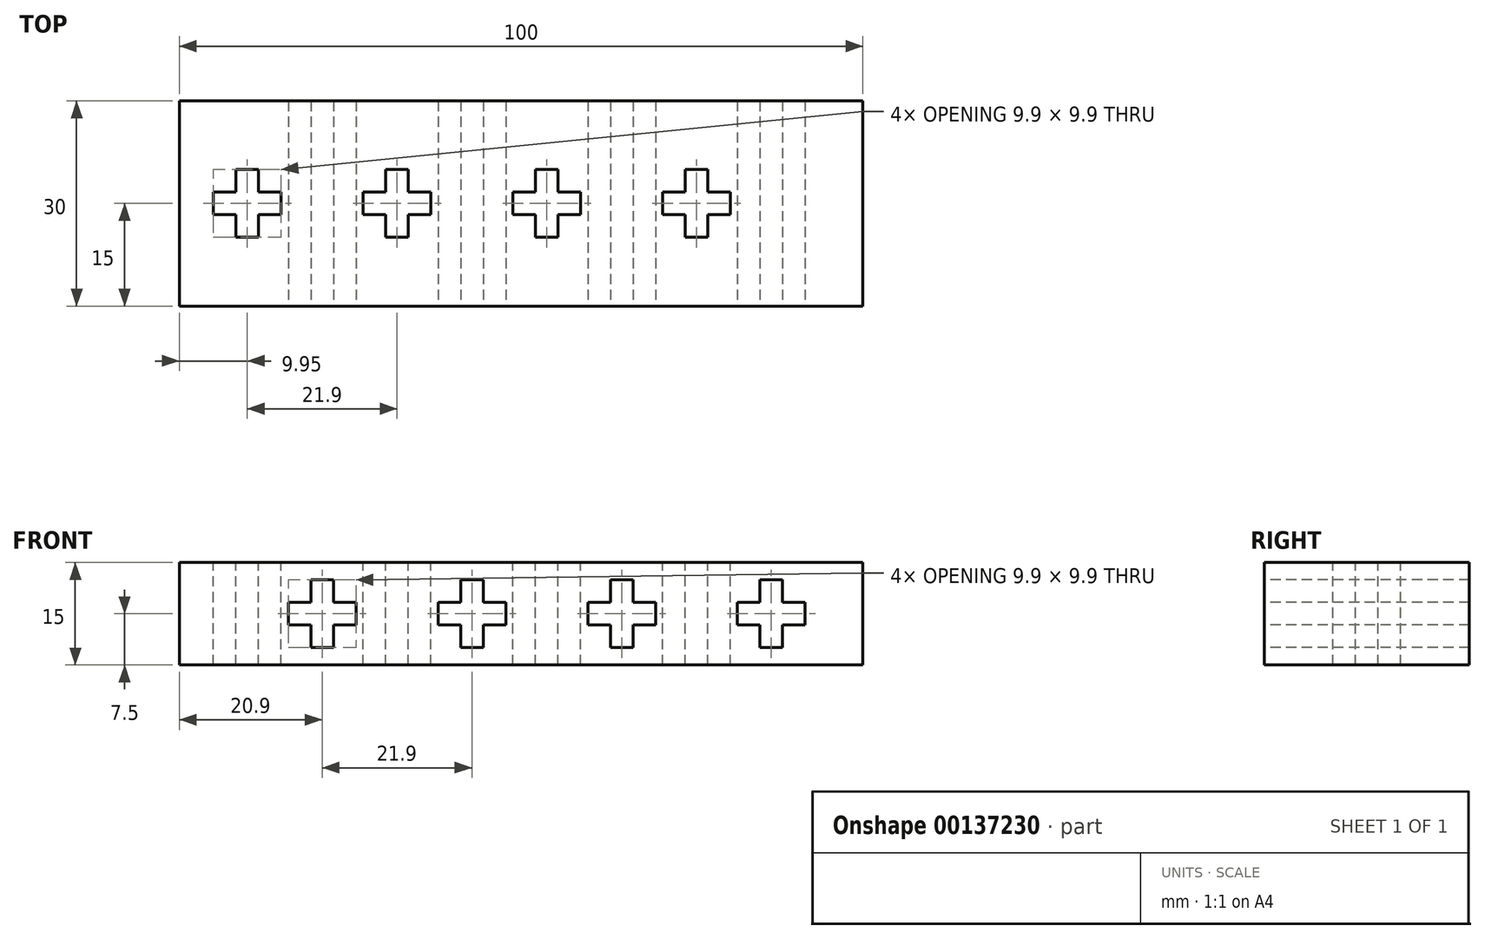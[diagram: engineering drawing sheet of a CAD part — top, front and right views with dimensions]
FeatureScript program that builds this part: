
annotation { "Feature Type Name" : "Feature", "Feature Type Description" : "" }
export const myFeature = defineFeature(function(context is Context, id is Id, definition is map)
    precondition{}
    {
        {
            var Q0;
            Q0=qCreatedBy(makeId("Top.planeOp"),FACE);
            var sketch = newSketch(context, id + "F0", { "sketchPlane" : qUnion([Q0])});
            skLineSegment(sketch, "E0.bottom", {"start": v(-50, 15) * mm, "end": v(50, 15) * mm});
            skLineSegment(sketch, "E0.top", {"start": v(-50, -15) * mm, "end": v(50, -15) * mm});
            skLineSegment(sketch, "E0.left", {"start": v(-50, 15) * mm, "end": v(-50, -15) * mm});
            skLineSegment(sketch, "E0.right", {"start": v(50, 15) * mm, "end": v(50, -15) * mm});
            skPoint(sketch, "E0.middle", {"position": v(0, 0) * mm});
            skSolve(sketch);
        }
        {
            var Q0;
            Q0 = qSketchRegion(id + "F0", true);
            extrude(context, id + "F1", {"entities" : qUnion([Q0]), "depth" : 15 * mm});
        }
        {
            var Q0;
            Q0=makeQuery(id+"F1.opExtrude","CAP_FACE",FACE,{"disambiguationData":[OSD([sQuery(id+"F0.wireOp",EDGE,"E0.bottom"),sQuery(id+"F0.wireOp",EDGE,"E0.top"),sQuery(id+"F0.wireOp",EDGE,"E0.left"),sQuery(id+"F0.wireOp",EDGE,"E0.right")])],"isStart":false});
            var sketch = newSketch(context, id + "F2", { "sketchPlane" : qUnion([Q0])});
            skLineSegment(sketch, "E1.bottom", {"start": v(-41.7, 4.95) * mm, "end": v(-38.4, 4.95) * mm});
            skLineSegment(sketch, "E1.top", {"start": v(-41.7, -4.95) * mm, "end": v(-38.4, -4.95) * mm});
            skLineSegment(sketch, "E1.left", {"start": v(-41.7, 4.95) * mm, "end": v(-41.7, 1.65) * mm});
            skLineSegment(sketch, "E1.right", {"start": v(-38.4, 4.95) * mm, "end": v(-38.4, 1.65) * mm});
            skPoint(sketch, "E1.middle", {"position": v(-40.05, 0) * mm});
            skLineSegment(sketch, "E2.bottom", {"start": v(-45, 1.65) * mm, "end": v(-41.7, 1.65) * mm});
            skLineSegment(sketch, "E2.top", {"start": v(-45, -1.65) * mm, "end": v(-41.7, -1.65) * mm});
            skLineSegment(sketch, "E2.left", {"start": v(-45, 1.65) * mm, "end": v(-45, -1.65) * mm});
            skLineSegment(sketch, "E2.right", {"start": v(-35.1, 1.65) * mm, "end": v(-35.1, -1.65) * mm});
            skLineSegment(sketch, "E3.trimOffspring", {"start": v(-41.7, -1.65) * mm, "end": v(-41.7, -4.95) * mm});
            skLineSegment(sketch, "E4.trimOffspring", {"start": v(-38.4, 1.65) * mm, "end": v(-35.1, 1.65) * mm});
            skLineSegment(sketch, "E5.trimOffspring", {"start": v(-38.4, -1.65) * mm, "end": v(-38.4, -4.95) * mm});
            skLineSegment(sketch, "E6.trimOffspring", {"start": v(-38.4, -1.65) * mm, "end": v(-35.1, -1.65) * mm});
            skPoint(sketch, "E7.1.0.0", {"position": v(-18.15, 0) * mm});
            skLineSegment(sketch, "E7.1.0.1", {"start": v(-23.1, -1.65) * mm, "end": v(-19.8, -1.65) * mm});
            skLineSegment(sketch, "E7.1.0.2", {"start": v(-16.5, -1.65) * mm, "end": v(-13.2, -1.65) * mm});
            skLineSegment(sketch, "E7.1.0.3", {"start": v(-16.5, -1.65) * mm, "end": v(-16.5, -4.95) * mm});
            skLineSegment(sketch, "E7.1.0.4", {"start": v(-16.5, 4.95) * mm, "end": v(-16.5, 1.65) * mm});
            skLineSegment(sketch, "E7.1.0.5", {"start": v(-19.8, 4.95) * mm, "end": v(-19.8, 1.65) * mm});
            skLineSegment(sketch, "E7.1.0.6", {"start": v(-19.8, -4.95) * mm, "end": v(-16.5, -4.95) * mm});
            skLineSegment(sketch, "E7.1.0.7", {"start": v(-19.8, 4.95) * mm, "end": v(-16.5, 4.95) * mm});
            skLineSegment(sketch, "E7.1.0.8", {"start": v(-16.5, 1.65) * mm, "end": v(-13.2, 1.65) * mm});
            skLineSegment(sketch, "E7.1.0.9", {"start": v(-23.1, 1.65) * mm, "end": v(-19.8, 1.65) * mm});
            skLineSegment(sketch, "E7.1.0.10", {"start": v(-19.8, -1.65) * mm, "end": v(-19.8, -4.95) * mm});
            skLineSegment(sketch, "E7.1.0.11", {"start": v(-23.1, 1.65) * mm, "end": v(-23.1, -1.65) * mm});
            skLineSegment(sketch, "E7.1.0.12", {"start": v(-13.2, 1.65) * mm, "end": v(-13.2, -1.65) * mm});
            skPoint(sketch, "E7.1.0.13", {"position": v(-18.15, 0) * mm});
            skPoint(sketch, "E7.2.0.0", {"position": v(3.75, 0) * mm});
            skLineSegment(sketch, "E7.2.0.1", {"start": v(-1.2, -1.65) * mm, "end": v(2.1, -1.65) * mm});
            skLineSegment(sketch, "E7.2.0.2", {"start": v(5.4, -1.65) * mm, "end": v(8.7, -1.65) * mm});
            skLineSegment(sketch, "E7.2.0.3", {"start": v(5.4, -1.65) * mm, "end": v(5.4, -4.95) * mm});
            skLineSegment(sketch, "E7.2.0.4", {"start": v(5.4, 4.95) * mm, "end": v(5.4, 1.65) * mm});
            skLineSegment(sketch, "E7.2.0.5", {"start": v(2.1, 4.95) * mm, "end": v(2.1, 1.65) * mm});
            skLineSegment(sketch, "E7.2.0.6", {"start": v(2.1, -4.95) * mm, "end": v(5.4, -4.95) * mm});
            skLineSegment(sketch, "E7.2.0.7", {"start": v(2.1, 4.95) * mm, "end": v(5.4, 4.95) * mm});
            skLineSegment(sketch, "E7.2.0.8", {"start": v(5.4, 1.65) * mm, "end": v(8.7, 1.65) * mm});
            skLineSegment(sketch, "E7.2.0.9", {"start": v(-1.2, 1.65) * mm, "end": v(2.1, 1.65) * mm});
            skLineSegment(sketch, "E7.2.0.10", {"start": v(2.1, -1.65) * mm, "end": v(2.1, -4.95) * mm});
            skLineSegment(sketch, "E7.2.0.11", {"start": v(-1.2, 1.65) * mm, "end": v(-1.2, -1.65) * mm});
            skLineSegment(sketch, "E7.2.0.12", {"start": v(8.7, 1.65) * mm, "end": v(8.7, -1.65) * mm});
            skPoint(sketch, "E7.2.0.13", {"position": v(3.75, 0) * mm});
            skPoint(sketch, "E7.3.0.0", {"position": v(25.65, 0) * mm});
            skLineSegment(sketch, "E7.3.0.1", {"start": v(20.7, -1.65) * mm, "end": v(24, -1.65) * mm});
            skLineSegment(sketch, "E7.3.0.2", {"start": v(27.3, -1.65) * mm, "end": v(30.6, -1.65) * mm});
            skLineSegment(sketch, "E7.3.0.3", {"start": v(27.3, -1.65) * mm, "end": v(27.3, -4.95) * mm});
            skLineSegment(sketch, "E7.3.0.4", {"start": v(27.3, 4.95) * mm, "end": v(27.3, 1.65) * mm});
            skLineSegment(sketch, "E7.3.0.5", {"start": v(24, 4.95) * mm, "end": v(24, 1.65) * mm});
            skLineSegment(sketch, "E7.3.0.6", {"start": v(24, -4.95) * mm, "end": v(27.3, -4.95) * mm});
            skLineSegment(sketch, "E7.3.0.7", {"start": v(24, 4.95) * mm, "end": v(27.3, 4.95) * mm});
            skLineSegment(sketch, "E7.3.0.8", {"start": v(27.3, 1.65) * mm, "end": v(30.6, 1.65) * mm});
            skLineSegment(sketch, "E7.3.0.9", {"start": v(20.7, 1.65) * mm, "end": v(24, 1.65) * mm});
            skLineSegment(sketch, "E7.3.0.10", {"start": v(24, -1.65) * mm, "end": v(24, -4.95) * mm});
            skLineSegment(sketch, "E7.3.0.11", {"start": v(20.7, 1.65) * mm, "end": v(20.7, -1.65) * mm});
            skLineSegment(sketch, "E7.3.0.12", {"start": v(30.6, 1.65) * mm, "end": v(30.6, -1.65) * mm});
            skPoint(sketch, "E7.3.0.13", {"position": v(25.65, 0) * mm});
            skLineSegment(sketch, "E7.direction1", {"start": v(-45, 1.65) * mm, "end": v(-23.1, 1.65) * mm, "construction": true});
            skSolve(sketch);
        }
        {
            var Q0;
            Q0 = qSketchRegion(id + "F2", true);
            extrude(context, id + "F3", {"entities" : qUnion([Q0]), "operationType" : NewBodyOperationType.REMOVE, "endBound" : BoundingType.THROUGH_ALL, "oppositeDirection" : true, "depth" : 25 * mm});
        }
        {
            var Q0;
            Q0=makeQuery(id+"F1.opExtrude","SWEPT_FACE",FACE,{"disambiguationData":[OSD([sQuery(id+"F0.wireOp",EDGE,"E0.top")])]});
            var sketch = newSketch(context, id + "F4", { "sketchPlane" : qUnion([Q0])});
            skLineSegment(sketch, "E8", {"start": v(-50, 7.5) * mm, "end": v(50, 7.5) * mm, "construction": true});
            skLineSegment(sketch, "E9.bottom", {"start": v(-30.75, 12.45) * mm, "end": v(-27.45, 12.45) * mm});
            skLineSegment(sketch, "E9.top", {"start": v(-30.75, 2.55) * mm, "end": v(-27.45, 2.55) * mm});
            skLineSegment(sketch, "E9.left", {"start": v(-30.75, 12.45) * mm, "end": v(-30.75, 9.15) * mm});
            skPoint(sketch, "E9.middle", {"position": v(-29.1, 7.5) * mm});
            skLineSegment(sketch, "E10.bottom", {"start": v(-34.05, 9.15) * mm, "end": v(-30.75, 9.15) * mm});
            skLineSegment(sketch, "E10.top", {"start": v(-34.05, 5.85) * mm, "end": v(-30.75, 5.85) * mm});
            skLineSegment(sketch, "E10.left", {"start": v(-34.05, 9.15) * mm, "end": v(-34.05, 5.85) * mm});
            skLineSegment(sketch, "E10.right", {"start": v(-24.15, 9.15) * mm, "end": v(-24.15, 5.85) * mm});
            skLineSegment(sketch, "E11.trimOffspring", {"start": v(-30.75, 5.85) * mm, "end": v(-30.75, 2.55) * mm});
            skLineSegment(sketch, "E12.trimOffspring", {"start": v(-27.45, 9.15) * mm, "end": v(-24.15, 9.15) * mm});
            skLineSegment(sketch, "E13.trimOffspring", {"start": v(-27.45, 5.85) * mm, "end": v(-27.45, 2.55) * mm});
            skLineSegment(sketch, "E14.trimOffspring", {"start": v(-27.45, 5.85) * mm, "end": v(-24.15, 5.85) * mm});
            skLineSegment(sketch, "E15", {"start": v(-27.45, 12.45) * mm, "end": v(-27.45, 9.15) * mm});
            skPoint(sketch, "E16.1.0.0", {"position": v(-7.2, 7.5) * mm});
            skLineSegment(sketch, "E16.1.0.1", {"start": v(-12.15, 9.15) * mm, "end": v(-12.15, 5.85) * mm});
            skLineSegment(sketch, "E16.1.0.2", {"start": v(-5.55, 12.45) * mm, "end": v(-5.55, 9.15) * mm});
            skLineSegment(sketch, "E16.1.0.3", {"start": v(-12.15, 9.15) * mm, "end": v(-8.85, 9.15) * mm});
            skLineSegment(sketch, "E16.1.0.4", {"start": v(-5.55, 5.85) * mm, "end": v(-2.25, 5.85) * mm});
            skLineSegment(sketch, "E16.1.0.5", {"start": v(-8.85, 12.45) * mm, "end": v(-5.55, 12.45) * mm});
            skLineSegment(sketch, "E16.1.0.6", {"start": v(-5.55, 5.85) * mm, "end": v(-5.55, 2.55) * mm});
            skLineSegment(sketch, "E16.1.0.7", {"start": v(-8.85, 12.45) * mm, "end": v(-8.85, 9.15) * mm});
            skLineSegment(sketch, "E16.1.0.8", {"start": v(-5.55, 9.15) * mm, "end": v(-2.25, 9.15) * mm});
            skLineSegment(sketch, "E16.1.0.9", {"start": v(-8.85, 5.85) * mm, "end": v(-8.85, 2.55) * mm});
            skLineSegment(sketch, "E16.1.0.10", {"start": v(-2.25, 9.15) * mm, "end": v(-2.25, 5.85) * mm});
            skLineSegment(sketch, "E16.1.0.11", {"start": v(-12.15, 5.85) * mm, "end": v(-8.85, 5.85) * mm});
            skLineSegment(sketch, "E16.1.0.12", {"start": v(-8.85, 2.55) * mm, "end": v(-5.55, 2.55) * mm});
            skPoint(sketch, "E16.1.0.13", {"position": v(-7.2, 7.5) * mm});
            skPoint(sketch, "E16.2.0.0", {"position": v(14.7, 7.5) * mm});
            skLineSegment(sketch, "E16.2.0.1", {"start": v(9.75, 9.15) * mm, "end": v(9.75, 5.85) * mm});
            skLineSegment(sketch, "E16.2.0.2", {"start": v(16.35, 12.45) * mm, "end": v(16.35, 9.15) * mm});
            skLineSegment(sketch, "E16.2.0.3", {"start": v(9.75, 9.15) * mm, "end": v(13.05, 9.15) * mm});
            skLineSegment(sketch, "E16.2.0.4", {"start": v(16.35, 5.85) * mm, "end": v(19.65, 5.85) * mm});
            skLineSegment(sketch, "E16.2.0.5", {"start": v(13.05, 12.45) * mm, "end": v(16.35, 12.45) * mm});
            skLineSegment(sketch, "E16.2.0.6", {"start": v(16.35, 5.85) * mm, "end": v(16.35, 2.55) * mm});
            skLineSegment(sketch, "E16.2.0.7", {"start": v(13.05, 12.45) * mm, "end": v(13.05, 9.15) * mm});
            skLineSegment(sketch, "E16.2.0.8", {"start": v(16.35, 9.15) * mm, "end": v(19.65, 9.15) * mm});
            skLineSegment(sketch, "E16.2.0.9", {"start": v(13.05, 5.85) * mm, "end": v(13.05, 2.55) * mm});
            skLineSegment(sketch, "E16.2.0.10", {"start": v(19.65, 9.15) * mm, "end": v(19.65, 5.85) * mm});
            skLineSegment(sketch, "E16.2.0.11", {"start": v(9.75, 5.85) * mm, "end": v(13.05, 5.85) * mm});
            skLineSegment(sketch, "E16.2.0.12", {"start": v(13.05, 2.55) * mm, "end": v(16.35, 2.55) * mm});
            skPoint(sketch, "E16.2.0.13", {"position": v(14.7, 7.5) * mm});
            skPoint(sketch, "E16.3.0.0", {"position": v(36.6, 7.5) * mm});
            skLineSegment(sketch, "E16.3.0.1", {"start": v(31.65, 9.15) * mm, "end": v(31.65, 5.85) * mm});
            skLineSegment(sketch, "E16.3.0.2", {"start": v(38.25, 12.45) * mm, "end": v(38.25, 9.15) * mm});
            skLineSegment(sketch, "E16.3.0.3", {"start": v(31.65, 9.15) * mm, "end": v(34.95, 9.15) * mm});
            skLineSegment(sketch, "E16.3.0.4", {"start": v(38.25, 5.85) * mm, "end": v(41.55, 5.85) * mm});
            skLineSegment(sketch, "E16.3.0.5", {"start": v(34.95, 12.45) * mm, "end": v(38.25, 12.45) * mm});
            skLineSegment(sketch, "E16.3.0.6", {"start": v(38.25, 5.85) * mm, "end": v(38.25, 2.55) * mm});
            skLineSegment(sketch, "E16.3.0.7", {"start": v(34.95, 12.45) * mm, "end": v(34.95, 9.15) * mm});
            skLineSegment(sketch, "E16.3.0.8", {"start": v(38.25, 9.15) * mm, "end": v(41.55, 9.15) * mm});
            skLineSegment(sketch, "E16.3.0.9", {"start": v(34.95, 5.85) * mm, "end": v(34.95, 2.55) * mm});
            skLineSegment(sketch, "E16.3.0.10", {"start": v(41.55, 9.15) * mm, "end": v(41.55, 5.85) * mm});
            skLineSegment(sketch, "E16.3.0.11", {"start": v(31.65, 5.85) * mm, "end": v(34.95, 5.85) * mm});
            skLineSegment(sketch, "E16.3.0.12", {"start": v(34.95, 2.55) * mm, "end": v(38.25, 2.55) * mm});
            skPoint(sketch, "E16.3.0.13", {"position": v(36.6, 7.5) * mm});
            skLineSegment(sketch, "E16.direction1", {"start": v(-24.15, 5.85) * mm, "end": v(-2.25, 5.85) * mm, "construction": true});
            skSolve(sketch);
        }
        {
            var Q0;
            Q0 = qSketchRegion(id + "F4", true);
            extrude(context, id + "F5", {"entities" : qUnion([Q0]), "operationType" : NewBodyOperationType.REMOVE, "endBound" : BoundingType.THROUGH_ALL, "oppositeDirection" : true, "depth" : 25 * mm});
        }
    });
